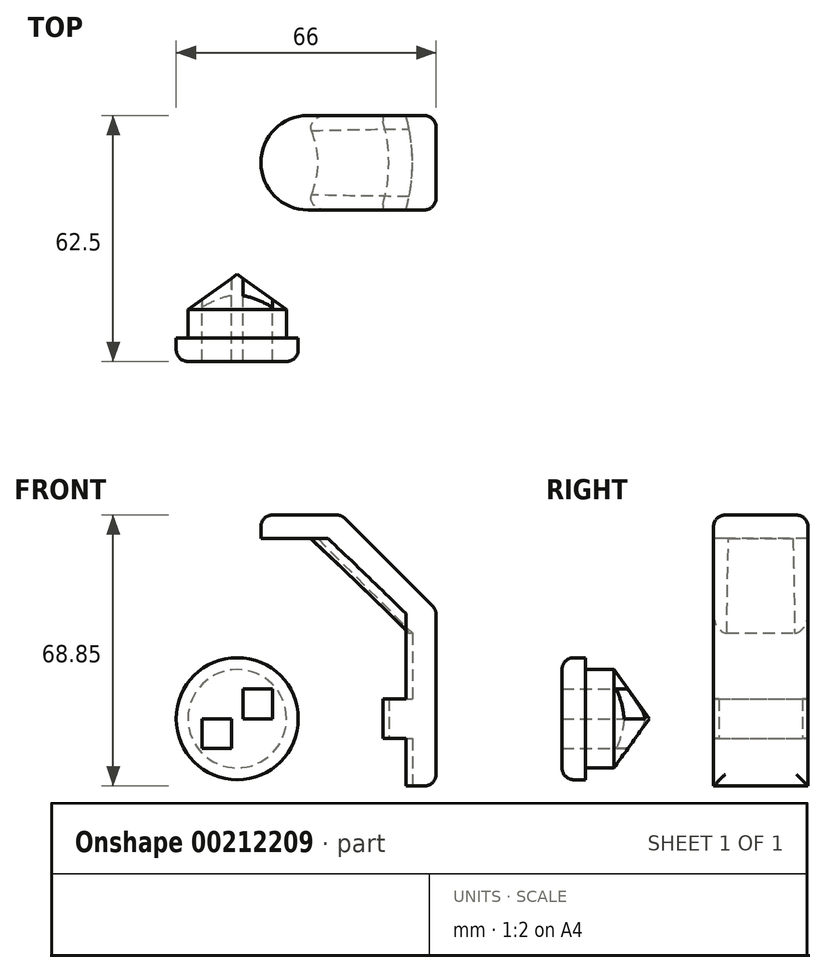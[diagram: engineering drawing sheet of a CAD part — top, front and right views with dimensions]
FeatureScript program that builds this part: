
annotation { "Feature Type Name" : "Feature", "Feature Type Description" : "" }
export const myFeature = defineFeature(function(context is Context, id is Id, definition is map)
    precondition{}
    {
        {
            assignVariable(context, id + "F0", {"name" : "ballWidth", "anyValue" : 77});
        }
        {
            assignVariable(context, id + "F1", {"name" : "shellDepth", "anyValue" : 6});
        }
        {
            assignVariable(context, id + "F2", {"name" : "buttonDia", "anyValue" : 25});
        }
        {
            assignVariable(context, id + "F3", {"name" : "ringHeight", "anyValue" : 10});
        }
        {
            assignVariable(context, id + "F4", {"name" : "edge", "anyValue" : getVariable(context, 'shellDepth') / 2});
        }
        {
            assignVariable(context, id + "F5", {"name" : "tolerance", "anyValue" : 1.25});
        }
        {
            assignVariable(context, id + "F6", {"name" : "scraperDepth", "anyValue" : 12});
        }
        {
            var Q0;
            Q0=qCreatedBy(makeId("Top.planeOp"),FACE);
            var sketch = newSketch(context, id + "F7", { "sketchPlane" : qUnion([Q0])});
            skCircle(sketch, "E0", {"center": v(0, 0) * mm, "radius": 38.5 * mm});
            skCircle(sketch, "E1.0", {"center": v(0, 0) * mm, "radius": 44.5 * mm});
            skSolve(sketch);
        }
        {
            var Q0;
            Q0=qCreatedBy(makeId("Front.planeOp"),FACE);
            var sketch = newSketch(context, id + "F8", { "sketchPlane" : qUnion([Q0])});
            skLineSegment(sketch, "E2", {"start": v(0, 0) * mm, "end": v(0, 44.5) * mm, "construction": true});
            skCircle(sketch, "E3", {"center": v(0, 44.5) * mm, "radius": 12.5 * mm});
            skCircle(sketch, "E4", {"center": v(0, 44.5) * mm, "radius": 38.5 * mm});
            skCircle(sketch, "E5.0", {"center": v(0, 44.5) * mm, "radius": 15.5 * mm});
            skCircle(sketch, "E6.0", {"center": v(0, 44.5) * mm, "radius": 13.75 * mm});
            skSolve(sketch);
        }
        {
            var Q0;
            Q0=qCreatedBy(makeId("Front.planeOp"),FACE);
            var sketch = newSketch(context, id + "F9", { "sketchPlane" : qUnion([Q0])});
            skLineSegment(sketch, "E7", {"start": v(0, 44.5) * mm, "end": v(50.5, 44.5) * mm, "construction": true});
            skLineSegment(sketch, "E8", {"start": v(50.5, 44.5) * mm, "end": v(50.5, 96.25) * mm});
            skLineSegment(sketch, "E9", {"start": v(50.5, 96.25) * mm, "end": v(6, 96.25) * mm});
            skLineSegment(sketch, "E10", {"start": v(6, 96.25) * mm, "end": v(6, 90.25) * mm});
            skLineSegment(sketch, "E11", {"start": v(6, 90.25) * mm, "end": v(44.5, 90.25) * mm});
            skLineSegment(sketch, "E12", {"start": v(44.5, 90.25) * mm, "end": v(44.5, 49.5) * mm});
            skLineSegment(sketch, "E13", {"start": v(44.5, 49.5) * mm, "end": v(37, 49.5) * mm});
            skLineSegment(sketch, "E14", {"start": v(44.5, 39.5) * mm, "end": v(37, 39.5) * mm});
            skLineSegment(sketch, "E15", {"start": v(37, 49.5) * mm, "end": v(37, 39.5) * mm});
            skLineSegment(sketch, "E16", {"start": v(37, 49.5) * mm, "end": v(37, 90.25) * mm});
            skLineSegment(sketch, "E17", {"start": v(0, 0) * mm, "end": v(0, 44.5) * mm, "construction": true});
            skLineSegment(sketch, "E18", {"start": v(50.5, 44.5) * mm, "end": v(50.5, 27.4) * mm});
            skLineSegment(sketch, "E19", {"start": v(50.5, 27.4) * mm, "end": v(37, 27.4) * mm});
            skLineSegment(sketch, "E20", {"start": v(44.5, 39.5) * mm, "end": v(44.5, 27.4) * mm});
            skPoint(sketch, "E20.endSnap0", {"position": v(43.75, 27.4) * mm});
            skLineSegment(sketch, "E21", {"start": v(37, 39.5) * mm, "end": v(37, 27.4) * mm});
            skSolve(sketch);
        }
        {
            var Q0;
            Q0=qCreatedBy(makeId("Front.planeOp"),FACE);
            var sketch = newSketch(context, id + "F10", { "sketchPlane" : qUnion([Q0])});
            skLineSegment(sketch, "E22", {"start": v(0, 0) * mm, "end": v(0, 44.5) * mm, "construction": true});
            skLineSegment(sketch, "E23", {"start": v(0, 44.5) * mm, "end": v(-1.5, 44.5) * mm, "construction": true});
            skLineSegment(sketch, "E24.bottom", {"start": v(-1.5, 44.5) * mm, "end": v(-9, 44.5) * mm});
            skLineSegment(sketch, "E24.top", {"start": v(-1.5, 37) * mm, "end": v(-9, 37) * mm});
            skLineSegment(sketch, "E24.left", {"start": v(-1.5, 44.5) * mm, "end": v(-1.5, 37) * mm});
            skLineSegment(sketch, "E24.right", {"start": v(-9, 44.5) * mm, "end": v(-9, 37) * mm});
            skLineSegment(sketch, "E25", {"start": v(0, 44.5) * mm, "end": v(1.5, 44.5) * mm, "construction": true});
            skLineSegment(sketch, "E26.bottom", {"start": v(1.5, 44.5) * mm, "end": v(9, 44.5) * mm});
            skLineSegment(sketch, "E26.top", {"start": v(1.5, 52) * mm, "end": v(9, 52) * mm});
            skLineSegment(sketch, "E26.left", {"start": v(1.5, 44.5) * mm, "end": v(1.5, 52) * mm});
            skLineSegment(sketch, "E26.right", {"start": v(9, 44.5) * mm, "end": v(9, 52) * mm});
            skSolve(sketch);
        }
        {
            var Q0;
            Q0=makeQuery(id+"F7.imprint","IMPRINT",FACE,{"disambiguationData":[TD([[makeQuery(id+"F7.imprint","IMPRINT",EDGE,{"derivedFrom":sQuery(id+"F7.wireOp",EDGE,"E0")}),1.0]])]});
            extrude(context, id + "F11", {"entities" : qUnion([Q0]), "depth" : (getVariable(context, 'ballWidth') + getVariable(context, 'shellDepth')) * mm, "hasSecondDirection" : true, "secondDirectionOppositeDirection" : false, "secondDirectionDepth" : (getVariable(context, 'shellDepth')) * mm});
        }
        {
            var Q0;
            Q0=makeQuery(id+"F11.opExtrude","CAP_EDGE",EDGE,{"disambiguationData":[OSD([sQuery(id+"F7.wireOp",EDGE,"E0")])],"isStart":false});
            var Q1;
            Q1=makeQuery(id+"F11.opExtrude","CAP_EDGE",EDGE,{"disambiguationData":[OSD([sQuery(id+"F7.wireOp",EDGE,"E0")])],"isStart":true});
            fillet(context, id + "F12", {"entities" : qUnion([Q0, Q1]), "radius" : (getVariable(context, 'ballWidth') / 2) * mm, "tangentPropagation" : true, "allowEdgeOverflow" : false});
        }
        {
            var Q0;
            Q0=makeQuery(id+"F8.imprint","IMPRINT",FACE,{"disambiguationData":[TD([[makeQuery(id+"F8.imprint","IMPRINT",EDGE,{"derivedFrom":sQuery(id+"F8.wireOp",EDGE,"E3")}),1.0]])]});
            var Q1;
            Q1=makeQuery(id+"F8.imprint","IMPRINT",FACE,{"disambiguationData":[TD([[makeQuery(id+"F8.imprint","IMPRINT",EDGE,{"derivedFrom":sQuery(id+"F8.wireOp",EDGE,"E3")}),-1.0]])]});
            extrude(context, id + "F13", {"entities" : qUnion([Q0, Q1]), "operationType" : NewBodyOperationType.REMOVE, "depth" : (getVariable(context, 'ballWidth') / 2) * mm, "hasSecondDirection" : true, "secondDirectionOppositeDirection" : false, "secondDirectionDepth" : (getVariable(context, 'ballWidth') / 2 - 5) * mm});
        }
        {
            var Q0;
            Q0=makeQuery(id+"F7.imprint","IMPRINT",FACE,{"disambiguationData":[TD([[makeQuery(id+"F7.imprint","IMPRINT",EDGE,{"derivedFrom":sQuery(id+"F7.wireOp",EDGE,"E0")}),-1.0]])]});
            var Q1;
            Q1=makeQuery(id+"F7.imprint","IMPRINT",FACE,{"disambiguationData":[TD([[makeQuery(id+"F7.imprint","IMPRINT",EDGE,{"derivedFrom":sQuery(id+"F7.wireOp",EDGE,"E0")}),1.0]])]});
            extrude(context, id + "F14", {"entities" : qUnion([Q0, Q1]), "depth" : (getVariable(context, 'ballWidth') / 2 + getVariable(context, 'shellDepth')) * mm});
        }
        {
            var Q0;
            Q0=makeQuery(id+"F14.opExtrude","CAP_FACE",FACE,{"disambiguationData":[OSD([sQuery(id+"F7.wireOp",EDGE,"E1.0")])],"isStart":false});
            shell(context, id + "F15", {"entities" : qUnion([Q0]), "thickness" : (getVariable(context, 'shellDepth')) * mm});
        }
        {
            var Q0;
            {var subQ0=sQuery(id+"F7.wireOp",EDGE,"E1.0");Q0=makeQuery(id+"F15.opShell","OFFSET_EDGE",EDGE,{"disambiguationData":[OSD([subQ0]),TDD([makeQuery(id+"F14.opExtrude","CAP_EDGE",EDGE,{"disambiguationData":[OSD([subQ0])],"isStart":true})])]});}
            fillet(context, id + "F16", {"entities" : qUnion([Q0]), "radius" : (getVariable(context, 'ballWidth') / 2) * mm, "tangentPropagation" : true, "allowEdgeOverflow" : false});
        }
        {
            var Q0;
            Q0=makeQuery(id+"F8.imprint","IMPRINT",FACE,{"disambiguationData":[TD([[makeQuery(id+"F8.imprint","IMPRINT",EDGE,{"derivedFrom":sQuery(id+"F8.wireOp",EDGE,"E3")}),1.0]])]});
            var Q1;
            Q1=makeQuery(id+"F8.imprint","IMPRINT",FACE,{"disambiguationData":[TD([[makeQuery(id+"F8.imprint","IMPRINT",EDGE,{"derivedFrom":sQuery(id+"F8.wireOp",EDGE,"E3")}),-1.0]])]});
            extrude(context, id + "F17", {"entities" : qUnion([Q0, Q1]), "operationType" : NewBodyOperationType.REMOVE, "depth" : (getVariable(context, 'ballWidth') / 2 + getVariable(context, 'shellDepth')) * mm});
        }
        {
            var Q0;
            Q0=makeQuery(id+"F14.opExtrude","CAP_EDGE",EDGE,{"disambiguationData":[OSD([sQuery(id+"F7.wireOp",EDGE,"E1.0")])],"isStart":true});
            chamfer(context, id + "F18", {"entities" : qUnion([Q0]), "width" : (getVariable(context, 'shellDepth') * 4) * mm, "tangentPropagation" : true});
        }
        {
            var Q0;
            {var subQ0=sQuery(id+"F7.wireOp",EDGE,"E1.0");Q0=makeQuery(id+"F18.opChamfer","BLEND_EDGE",EDGE,{"blendedFrom":[makeQuery(id+"F14.opExtrude","CAP_EDGE",EDGE,{"disambiguationData":[OSD([subQ0])],"isStart":true}),makeQuery(id+"F14.opExtrude","SWEPT_FACE",FACE,{"disambiguationData":[OSD([subQ0])]})],"blendedInto":[makeQuery(id+"F14.opExtrude","SWEPT_FACE",FACE,{"disambiguationData":[OSD([subQ0])]})]});}
            fillet(context, id + "F19", {"entities" : qUnion([Q0]), "radius" : (getVariable(context, 'edge') * 3) * mm, "tangentPropagation" : true, "allowEdgeOverflow" : false});
        }
        {
            var Q0;
            Q0=makeQuery(id+"F7.imprint","IMPRINT",FACE,{"disambiguationData":[TD([[makeQuery(id+"F7.imprint","IMPRINT",EDGE,{"derivedFrom":sQuery(id+"F7.wireOp",EDGE,"E0")}),-1.0]])]});
            var Q1;
            Q1=makeQuery(id+"F7.imprint","IMPRINT",FACE,{"disambiguationData":[TD([[makeQuery(id+"F7.imprint","IMPRINT",EDGE,{"derivedFrom":sQuery(id+"F7.wireOp",EDGE,"E0")}),1.0]])]});
            extrude(context, id + "F20", {"entities" : qUnion([Q0, Q1]), "operationType" : NewBodyOperationType.REMOVE, "depth" : (getVariable(context, 'shellDepth') + getVariable(context, 'ballWidth') / 2) * mm, "hasSecondDirection" : true, "secondDirectionOppositeDirection" : false, "secondDirectionDepth" : (getVariable(context, 'shellDepth') + getVariable(context, 'ballWidth') / 2 - getVariable(context, 'ringHeight') / 2) * mm});
        }
        {
            var Q0;
            Q0=makeQuery(id+"F9.imprint","IMPRINT",FACE,{"disambiguationData":[TD([[makeQuery(id+"F9.imprint","IMPRINT",EDGE,{"derivedFrom":sQuery(id+"F9.wireOp",EDGE,"E8")}),1.0]])]});
            var Q1;
            {var subQ0=sQuery(id+"F9.wireOp",EDGE,"E12");Q1=makeQuery(id+"F9.imprint","IMPRINT",FACE,{"disambiguationData":[TD([[makeQuery(id+"F9.imprint","IMPRINT",EDGE,{"derivedFrom":subQ0}),-1.0]])]});}
            var Q2;
            {var subQ0=sQuery(id+"F9.wireOp",EDGE,"RWLq2zey-VeaJ-JO1z-50kb-arZdZIePhXVi");Q2=makeQuery(id+"F9.imprint","IMPRINT",FACE,{"disambiguationData":[TD([[makeQuery(id+"F9.imprint","IMPRINT",EDGE,{"derivedFrom":subQ0}),1.0]])]});}
            var Q3;
            Q3=makeQuery(id+"F9.imprint","IMPRINT",FACE,{"disambiguationData":[TD([[makeQuery(id+"F9.imprint","IMPRINT",EDGE,{"derivedFrom":sQuery(id+"F9.wireOp",EDGE,"E14")}),1.0]])]});
            extrude(context, id + "F21", {"entities" : qUnion([Q0, Q1, Q2, Q3]), "depth" : (getVariable(context, 'scraperDepth')) * mm, "hasSecondDirection" : true, "secondDirectionOppositeDirection" : true, "secondDirectionDepth" : (getVariable(context, 'scraperDepth')) * mm});
        }
        {
            var Q0;
            Q0=makeQuery(id+"F7.imprint","IMPRINT",FACE,{"disambiguationData":[TD([[makeQuery(id+"F7.imprint","IMPRINT",EDGE,{"derivedFrom":sQuery(id+"F7.wireOp",EDGE,"E0")}),-1.0]])]});
            var Q1;
            Q1=makeQuery(id+"F7.imprint","IMPRINT",FACE,{"disambiguationData":[TD([[makeQuery(id+"F7.imprint","IMPRINT",EDGE,{"derivedFrom":sQuery(id+"F7.wireOp",EDGE,"E0")}),1.0]])]});
            extrude(context, id + "F22", {"entities" : qUnion([Q0, Q1]), "operationType" : NewBodyOperationType.REMOVE, "depth" : (getVariable(context, 'shellDepth') + getVariable(context, 'ballWidth') / 2 - getVariable(context, 'ringHeight') / 2) * mm, "hasSecondDirection" : true, "secondDirectionOppositeDirection" : true, "secondDirectionDepth" : (getVariable(context, 'tolerance')) * mm});
        }
        {
            var Q0;
            Q0=makeQuery(id+"F7.imprint","IMPRINT",FACE,{"disambiguationData":[TD([[makeQuery(id+"F7.imprint","IMPRINT",EDGE,{"derivedFrom":sQuery(id+"F7.wireOp",EDGE,"E0")}),1.0]])]});
            var Q1;
            Q1=makeQuery(id+"F7.imprint","IMPRINT",FACE,{"disambiguationData":[TD([[makeQuery(id+"F7.imprint","IMPRINT",EDGE,{"derivedFrom":sQuery(id+"F7.wireOp",EDGE,"E0")}),-1.0]])]});
            extrude(context, id + "F23", {"entities" : qUnion([Q0, Q1]), "operationType" : NewBodyOperationType.REMOVE, "depth" : (getVariable(context, 'ballWidth') + getVariable(context, 'shellDepth') * 2 + getVariable(context, 'tolerance')) * mm, "hasSecondDirection" : true, "secondDirectionOppositeDirection" : false, "secondDirectionDepth" : (getVariable(context, 'ballWidth') / 2 + getVariable(context, 'shellDepth') + getVariable(context, 'ringHeight') / 2) * mm});
        }
        {
            var Q0;
            Q0=makeQuery(id+"F23.boolean.opBoolean","COPY",EDGE,{"derivedFrom":makeQuery(id+"F23.opExtrude","CAP_EDGE",EDGE,{"disambiguationData":[OSD([sQuery(id+"F7.wireOp",EDGE,"E1.0")])],"isStart":false})});
            var Q1;
            Q1=makeQuery(id+"F21.opExtrude","SWEPT_EDGE",EDGE,{"disambiguationData":[OSD([sQuery(id+"F9.wireOp",EDGE,"E8"),sQuery(id+"F9.wireOp",EDGE,"E9")])]});
            chamfer(context, id + "F24", {"entities" : qUnion([Q0, Q1]), "width" : (getVariable(context, 'shellDepth') * 4) * mm, "tangentPropagation" : true});
        }
        {
            var Q0;
            Q0=makeQuery(id+"F21.opExtrude","CAP_EDGE",EDGE,{"disambiguationData":[OSD([sQuery(id+"F9.wireOp",EDGE,"E10")])],"isStart":false});
            var Q1;
            Q1=makeQuery(id+"F21.opExtrude","CAP_EDGE",EDGE,{"disambiguationData":[OSD([sQuery(id+"F9.wireOp",EDGE,"E10")])],"isStart":true});
            fillet(context, id + "F25", {"entities" : qUnion([Q0, Q1]), "radius" : (getVariable(context, 'scraperDepth')) * mm, "tangentPropagation" : true, "allowEdgeOverflow" : false});
        }
        {
            var Q0;
            Q0=makeQuery(id+"F21.opExtrude","SWEPT_FACE",FACE,{"disambiguationData":[OSD([sQuery(id+"F9.wireOp",EDGE,"E9")])]});
            var Q1;
            Q1=makeQuery(id+"F21.opExtrude","SWEPT_FACE",FACE,{"disambiguationData":[OSD([sQuery(id+"F9.wireOp",EDGE,"E8"),sQuery(id+"F9.wireOp",EDGE,"s5j8ayal-mgPw-vfJ2-pD2J-bGzlMfYahmW3")])]});
            var Q2;
            Q2=makeQuery(id+"F21.opExtrude","SWEPT_FACE",FACE,{"disambiguationData":[OSD([sQuery(id+"F9.wireOp",EDGE,"jMFSWkzc-9W7W-heGW-MQlE-5a2P9RXpy2Zh")])]});
            var Q3;
            {var subQ0=sQuery(id+"F9.wireOp",EDGE,"E9");var subQ1=sQuery(id+"F9.wireOp",EDGE,"E8");Q3=makeQuery(id+"F24.opChamfer","BLEND_EDGE",EDGE,{"blendedFrom":[makeQuery(id+"F21.opExtrude","SWEPT_EDGE",EDGE,{"disambiguationData":[OSD([subQ1,subQ0])]}),makeQuery(id+"F21.opExtrude","CAP_FACE",FACE,{"disambiguationData":[OSD([subQ1,subQ0,sQuery(id+"F9.wireOp",EDGE,"E10"),sQuery(id+"F9.wireOp",EDGE,"E11"),sQuery(id+"F9.wireOp",EDGE,"E15"),sQuery(id+"F9.wireOp",EDGE,"E16"),sQuery(id+"F9.wireOp",EDGE,"E18"),sQuery(id+"F9.wireOp",EDGE,"E19"),sQuery(id+"F9.wireOp",EDGE,"E21")])],"isStart":true})],"blendedInto":[makeQuery(id+"F21.opExtrude","CAP_FACE",FACE,{"disambiguationData":[OSD([subQ1,subQ0,sQuery(id+"F9.wireOp",EDGE,"E10"),sQuery(id+"F9.wireOp",EDGE,"E11"),sQuery(id+"F9.wireOp",EDGE,"E15"),sQuery(id+"F9.wireOp",EDGE,"E16"),sQuery(id+"F9.wireOp",EDGE,"E18"),sQuery(id+"F9.wireOp",EDGE,"E19"),sQuery(id+"F9.wireOp",EDGE,"E21")])],"isStart":true})]});}
            var Q4;
            Q4=makeQuery(id+"F24.opChamfer","BLEND_EDGE",EDGE,{"blendedFrom":[makeQuery(id+"F23.boolean.opBoolean","COPY",EDGE,{"derivedFrom":makeQuery(id+"F23.opExtrude","CAP_EDGE",EDGE,{"disambiguationData":[OSD([sQuery(id+"F7.wireOp",EDGE,"E1.0")])],"isStart":false})}),makeQuery(id+"F21.opExtrude","CAP_FACE",FACE,{"disambiguationData":[OSD([sQuery(id+"F9.wireOp",EDGE,"E8"),sQuery(id+"F9.wireOp",EDGE,"E9"),sQuery(id+"F9.wireOp",EDGE,"E10"),sQuery(id+"F9.wireOp",EDGE,"E11"),sQuery(id+"F9.wireOp",EDGE,"E15"),sQuery(id+"F9.wireOp",EDGE,"E16"),sQuery(id+"F9.wireOp",EDGE,"E18"),sQuery(id+"F9.wireOp",EDGE,"E19"),sQuery(id+"F9.wireOp",EDGE,"E21")])],"isStart":true})],"blendedInto":[makeQuery(id+"F21.opExtrude","CAP_FACE",FACE,{"disambiguationData":[OSD([sQuery(id+"F9.wireOp",EDGE,"E8"),sQuery(id+"F9.wireOp",EDGE,"E9"),sQuery(id+"F9.wireOp",EDGE,"E10"),sQuery(id+"F9.wireOp",EDGE,"E11"),sQuery(id+"F9.wireOp",EDGE,"E15"),sQuery(id+"F9.wireOp",EDGE,"E16"),sQuery(id+"F9.wireOp",EDGE,"E18"),sQuery(id+"F9.wireOp",EDGE,"E19"),sQuery(id+"F9.wireOp",EDGE,"E21")])],"isStart":true})]});
            var Q5;
            {var subQ0=sQuery(id+"F9.wireOp",EDGE,"E9");var subQ1=sQuery(id+"F9.wireOp",EDGE,"E8");Q5=makeQuery(id+"F24.opChamfer","BLEND_EDGE",EDGE,{"blendedFrom":[makeQuery(id+"F21.opExtrude","SWEPT_EDGE",EDGE,{"disambiguationData":[OSD([subQ1,subQ0])]}),makeQuery(id+"F21.opExtrude","CAP_FACE",FACE,{"disambiguationData":[OSD([subQ1,subQ0,sQuery(id+"F9.wireOp",EDGE,"E10"),sQuery(id+"F9.wireOp",EDGE,"E11"),sQuery(id+"F9.wireOp",EDGE,"E15"),sQuery(id+"F9.wireOp",EDGE,"E16"),sQuery(id+"F9.wireOp",EDGE,"E18"),sQuery(id+"F9.wireOp",EDGE,"E19"),sQuery(id+"F9.wireOp",EDGE,"E21")])],"isStart":false})],"blendedInto":[makeQuery(id+"F21.opExtrude","CAP_FACE",FACE,{"disambiguationData":[OSD([subQ1,subQ0,sQuery(id+"F9.wireOp",EDGE,"E10"),sQuery(id+"F9.wireOp",EDGE,"E11"),sQuery(id+"F9.wireOp",EDGE,"E15"),sQuery(id+"F9.wireOp",EDGE,"E16"),sQuery(id+"F9.wireOp",EDGE,"E18"),sQuery(id+"F9.wireOp",EDGE,"E19"),sQuery(id+"F9.wireOp",EDGE,"E21")])],"isStart":false})]});}
            var Q6;
            Q6=makeQuery(id+"F24.opChamfer","BLEND_EDGE",EDGE,{"blendedFrom":[makeQuery(id+"F23.boolean.opBoolean","COPY",EDGE,{"derivedFrom":makeQuery(id+"F23.opExtrude","CAP_EDGE",EDGE,{"disambiguationData":[OSD([sQuery(id+"F7.wireOp",EDGE,"E1.0")])],"isStart":false})}),makeQuery(id+"F21.opExtrude","CAP_FACE",FACE,{"disambiguationData":[OSD([sQuery(id+"F9.wireOp",EDGE,"E8"),sQuery(id+"F9.wireOp",EDGE,"E9"),sQuery(id+"F9.wireOp",EDGE,"E10"),sQuery(id+"F9.wireOp",EDGE,"E11"),sQuery(id+"F9.wireOp",EDGE,"E15"),sQuery(id+"F9.wireOp",EDGE,"E16"),sQuery(id+"F9.wireOp",EDGE,"E18"),sQuery(id+"F9.wireOp",EDGE,"E19"),sQuery(id+"F9.wireOp",EDGE,"E21")])],"isStart":false})],"blendedInto":[makeQuery(id+"F21.opExtrude","CAP_FACE",FACE,{"disambiguationData":[OSD([sQuery(id+"F9.wireOp",EDGE,"E8"),sQuery(id+"F9.wireOp",EDGE,"E9"),sQuery(id+"F9.wireOp",EDGE,"E10"),sQuery(id+"F9.wireOp",EDGE,"E11"),sQuery(id+"F9.wireOp",EDGE,"E15"),sQuery(id+"F9.wireOp",EDGE,"E16"),sQuery(id+"F9.wireOp",EDGE,"E18"),sQuery(id+"F9.wireOp",EDGE,"E19"),sQuery(id+"F9.wireOp",EDGE,"E21")])],"isStart":false})]});
            fillet(context, id + "F26", {"entities" : qUnion([Q0, Q1, Q2, Q3, Q4, Q5, Q6]), "radius" : (getVariable(context, 'edge')) * mm, "tangentPropagation" : true, "allowEdgeOverflow" : false});
        }
        {
            var Q0;
            Q0=makeQuery(id+"F7.imprint","IMPRINT",FACE,{"disambiguationData":[TD([[makeQuery(id+"F7.imprint","IMPRINT",EDGE,{"derivedFrom":sQuery(id+"F7.wireOp",EDGE,"E0")}),1.0]])]});
            extrude(context, id + "F27", {"entities" : qUnion([Q0]), "operationType" : NewBodyOperationType.REMOVE, "depth" : (getVariable(context, 'ballWidth') / 2 + getVariable(context, 'shellDepth') * 2) * mm, "hasSecondDirection" : true, "secondDirectionOppositeDirection" : false, "secondDirectionDepth" : (getVariable(context, 'shellDepth')) * mm});
        }
        {
            var Q0;
            Q0=makeQuery(id+"F8.imprint","IMPRINT",FACE,{"disambiguationData":[TD([[makeQuery(id+"F8.imprint","IMPRINT",EDGE,{"derivedFrom":sQuery(id+"F8.wireOp",EDGE,"E3")}),-1.0]])]});
            var Q1;
            Q1=makeQuery(id+"F8.imprint","IMPRINT",FACE,{"disambiguationData":[TD([[makeQuery(id+"F8.imprint","IMPRINT",EDGE,{"derivedFrom":sQuery(id+"F8.wireOp",EDGE,"E3")}),1.0]])]});
            var Q2;
            Q2=makeQuery(id+"F8.imprint","IMPRINT",FACE,{"disambiguationData":[TD([[makeQuery(id+"F8.imprint","IMPRINT",EDGE,{"derivedFrom":sQuery(id+"F8.wireOp",EDGE,"E5.0")}),1.0]])]});
            extrude(context, id + "F28", {"entities" : qUnion([Q0, Q1, Q2]), "depth" : (getVariable(context, 'ballWidth') / 2 + getVariable(context, 'shellDepth') * 2) * mm, "hasSecondDirection" : true, "secondDirectionOppositeDirection" : false, "secondDirectionDepth" : (getVariable(context, 'ballWidth') / 2 + getVariable(context, 'shellDepth')) * mm});
        }
        {
            var Q0;
            Q0=makeQuery(id+"F8.imprint","IMPRINT",FACE,{"disambiguationData":[TD([[makeQuery(id+"F8.imprint","IMPRINT",EDGE,{"derivedFrom":sQuery(id+"F8.wireOp",EDGE,"E3")}),1.0]])]});
            extrude(context, id + "F29", {"entities" : qUnion([Q0]), "operationType" : NewBodyOperationType.ADD, "depth" : (getVariable(context, 'ballWidth') / 2 + getVariable(context, 'shellDepth')) * mm, "hasSecondDirection" : true, "secondDirectionOppositeDirection" : false, "secondDirectionDepth" : (getVariable(context, 'ballWidth') / 2 - getVariable(context, 'shellDepth') * 1.7) * mm});
        }
        {
            var Q0;
            Q0=makeQuery(id+"F29.opExtrude","CAP_EDGE",EDGE,{"disambiguationData":[OSD([sQuery(id+"F8.wireOp",EDGE,"E3")])],"isStart":true});
            chamfer(context, id + "F30", {"entities" : qUnion([Q0]), "chamferType" : ChamferType.TWO_OFFSETS, "width1" : (getVariable(context, 'shellDepth') * 1.5) * mm, "oppositeDirection" : false, "width2" : (getVariable(context, 'buttonDia') / 2) * mm, "tangentPropagation" : true});
        }
        {
            var Q0;
            Q0=makeQuery(id+"F10.imprint","IMPRINT",FACE,{"disambiguationData":[TD([[makeQuery(id+"F10.imprint","IMPRINT",EDGE,{"derivedFrom":sQuery(id+"F10.wireOp",EDGE,"E26.bottom")}),1.0]])]});
            var Q1;
            Q1=makeQuery(id+"F10.imprint","IMPRINT",FACE,{"disambiguationData":[TD([[makeQuery(id+"F10.imprint","IMPRINT",EDGE,{"derivedFrom":sQuery(id+"F10.wireOp",EDGE,"E24.bottom")}),1.0]])]});
            extrude(context, id + "F31", {"entities" : qUnion([Q0, Q1]), "operationType" : NewBodyOperationType.REMOVE, "depth" : (getVariable(context, 'ballWidth') / 2 + getVariable(context, 'shellDepth') * 2) * mm});
        }
        {
            var Q0;
            Q0=makeQuery(id+"F28.opExtrude","CAP_EDGE",EDGE,{"disambiguationData":[OSD([sQuery(id+"F8.wireOp",EDGE,"E5.0")])],"isStart":false});
            fillet(context, id + "F32", {"entities" : qUnion([Q0]), "radius" : (getVariable(context, 'edge')) * mm, "tangentPropagation" : true, "allowEdgeOverflow" : false});
        }
    });
